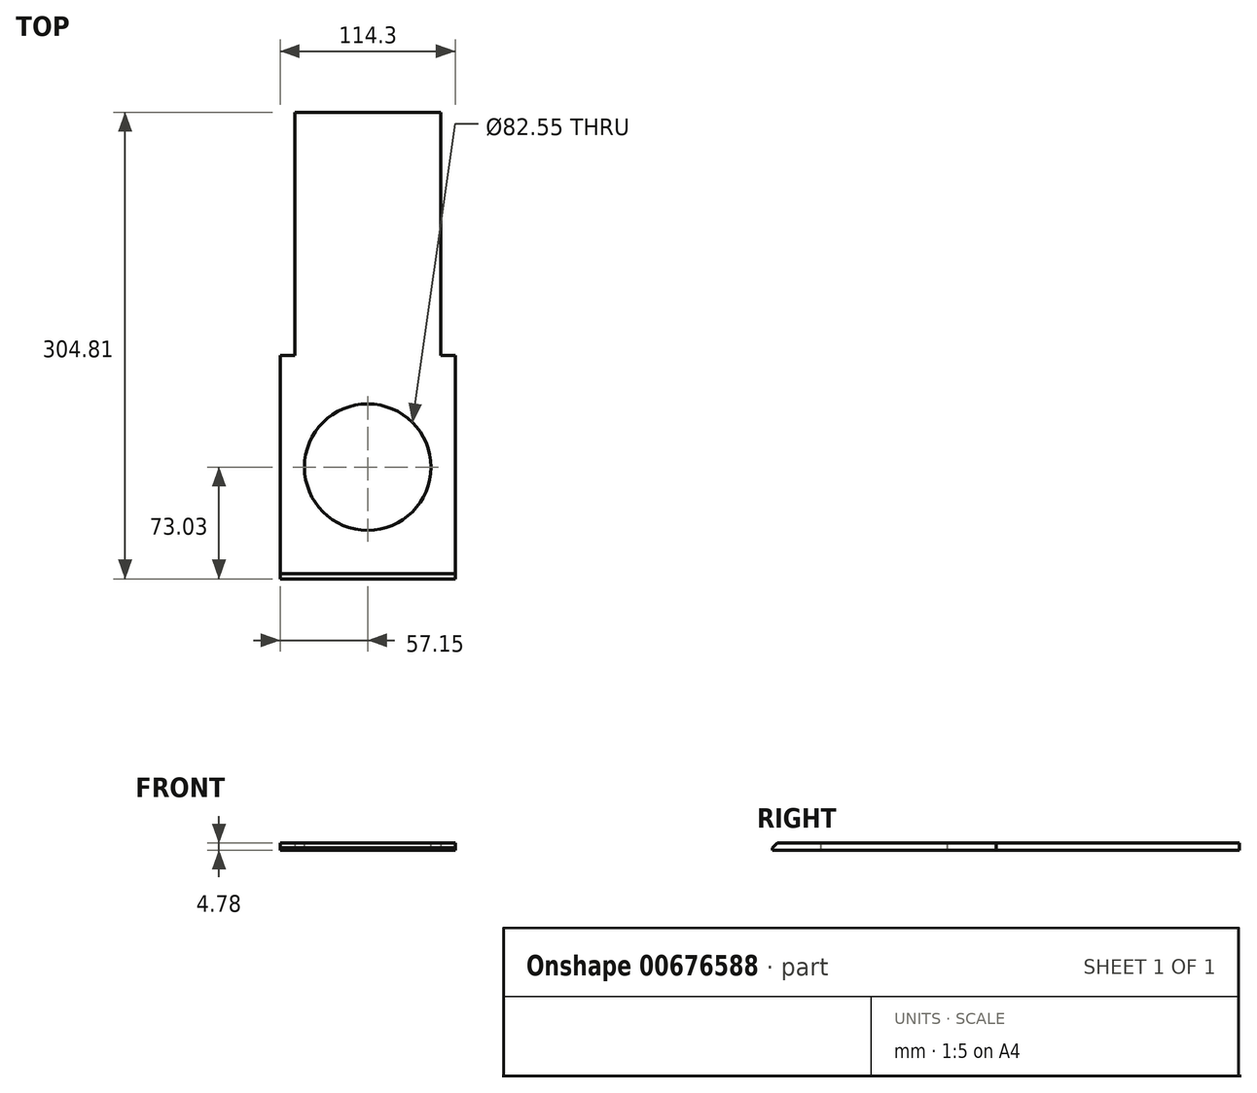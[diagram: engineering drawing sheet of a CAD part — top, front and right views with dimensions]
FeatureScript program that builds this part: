
annotation { "Feature Type Name" : "Feature", "Feature Type Description" : "" }
export const myFeature = defineFeature(function(context is Context, id is Id, definition is map)
    precondition{}
    {
        {
            var Q0;
            Q0=qCreatedBy(makeId("Top.planeOp"),FACE);
            var sketch = newSketch(context, id + "F0", { "sketchPlane" : qUnion([Q0])});
            skLineSegment(sketch, "E0.bottom", {"start": v(57.15, -73.02) * mm, "end": v(-57.15, -73.02) * mm});
            skLineSegment(sketch, "E0.top", {"start": v(57.15, 73.03) * mm, "end": v(-57.15, 73.02) * mm});
            skLineSegment(sketch, "E0.left", {"start": v(57.15, -73.02) * mm, "end": v(57.15, 73.02) * mm});
            skLineSegment(sketch, "E0.right", {"start": v(-57.15, -73.02) * mm, "end": v(-57.15, 73.03) * mm});
            skPoint(sketch, "E0.middle", {"position": v(0, 0) * mm});
            skLineSegment(sketch, "E1.bottom", {"start": v(-57.15, -73.02) * mm, "end": v(-50.8, -73.02) * mm});
            skLineSegment(sketch, "E1.top", {"start": v(-57.15, 60.32) * mm, "end": v(-50.8, 60.32) * mm});
            skLineSegment(sketch, "E1.left", {"start": v(-57.15, -73.02) * mm, "end": v(-57.15, 60.33) * mm});
            skLineSegment(sketch, "E1.right", {"start": v(-50.8, -73.02) * mm, "end": v(-50.8, 60.33) * mm});
            skLineSegment(sketch, "E2.bottom", {"start": v(57.15, -73.02) * mm, "end": v(50.8, -73.02) * mm});
            skLineSegment(sketch, "E2.top", {"start": v(57.15, 60.32) * mm, "end": v(50.8, 60.32) * mm});
            skLineSegment(sketch, "E2.left", {"start": v(57.15, -73.02) * mm, "end": v(57.15, 60.32) * mm});
            skLineSegment(sketch, "E2.right", {"start": v(50.8, -73.02) * mm, "end": v(50.8, 60.33) * mm});
            skLineSegment(sketch, "E3.bottom", {"start": v(-47.62, 73.02) * mm, "end": v(47.63, 73.02) * mm});
            skLineSegment(sketch, "E3.top", {"start": v(-47.62, 231.78) * mm, "end": v(47.63, 231.78) * mm});
            skLineSegment(sketch, "E3.left", {"start": v(-47.62, 73.03) * mm, "end": v(-47.62, 231.78) * mm});
            skLineSegment(sketch, "E3.right", {"start": v(47.63, 73.03) * mm, "end": v(47.63, 231.78) * mm});
            skSolve(sketch);
        }
        {
            var Q0;
            {var subQ11=sQuery(id+"F0.wireOp",EDGE,"E1.top");Q0=makeQuery(id+"F0.imprint","IMPRINT",FACE,{"disambiguationData":[TD([[makeQuery(id+"F0.imprint","IMPRINT",EDGE,{"derivedFrom":subQ11}),1.0]])]});}
            var Q1;
            Q1=makeQuery(id+"F0.imprint","IMPRINT",FACE,{"disambiguationData":[TD([[makeQuery(id+"F0.imprint","IMPRINT",EDGE,{"derivedFrom":sQuery(id+"F0.wireOp",EDGE,"E3.top")}),-1.0]])]});
            var Q2;
            {var subQ4=sQuery(id+"F0.wireOp",EDGE,"E1.top");Q2=makeQuery(id+"F0.imprint","IMPRINT",FACE,{"disambiguationData":[TD([[makeQuery(id+"F0.imprint","IMPRINT",EDGE,{"derivedFrom":subQ4}),-1.0]])]});}
            var Q3;
            {var subQ4=sQuery(id+"F0.wireOp",EDGE,"E2.top");Q3=makeQuery(id+"F0.imprint","IMPRINT",FACE,{"disambiguationData":[TD([[makeQuery(id+"F0.imprint","IMPRINT",EDGE,{"derivedFrom":subQ4}),1.0]])]});}
            extrude(context, id + "F1", {"entities" : qUnion([Q0, Q1, Q2, Q3]), "depth" : 4.78 * mm, "offsetDistance" : 25.4 * mm});
        }
        {
            var Q0;
            Q0=makeQuery(id+"F1.opExtrude","CAP_FACE",FACE,{"disambiguationData":[OSD([sQuery(id+"F0.wireOp",EDGE,"E0.bottom"),sQuery(id+"F0.wireOp",EDGE,"E0.top"),sQuery(id+"F0.wireOp",EDGE,"E0.left"),sQuery(id+"F0.wireOp",EDGE,"E0.right"),sQuery(id+"F0.wireOp",EDGE,"E3.top"),sQuery(id+"F0.wireOp",EDGE,"E3.left"),sQuery(id+"F0.wireOp",EDGE,"E3.right")])],"isStart":false});
            var sketch = newSketch(context, id + "F2", { "sketchPlane" : qUnion([Q0])});
            skCircle(sketch, "E4", {"center": v(0, 0) * mm, "radius": 41.28 * mm});
            skLineSegment(sketch, "E5.0", {"start": v(57.15, -73.02) * mm, "end": v(-57.15, -73.02) * mm});
            skSolve(sketch);
        }
        {
            var Q0;
            Q0 = qSketchRegion(id + "F2", true);
            extrude(context, id + "F3", {"entities" : qUnion([Q0]), "operationType" : NewBodyOperationType.REMOVE, "oppositeDirection" : true, "depth" : 25.4 * mm, "offsetDistance" : 25.4 * mm});
        }
        {
            var Q0;
            Q0=makeQuery(id+"F1.opExtrude","CAP_EDGE",EDGE,{"disambiguationData":[OSD([sQuery(id+"F0.wireOp",EDGE,"E0.bottom")])],"isStart":false});
            chamfer(context, id + "F4", {"entities" : qUnion([Q0]), "width" : 3.3 * mm, "tangentPropagation" : true});
        }
    });
